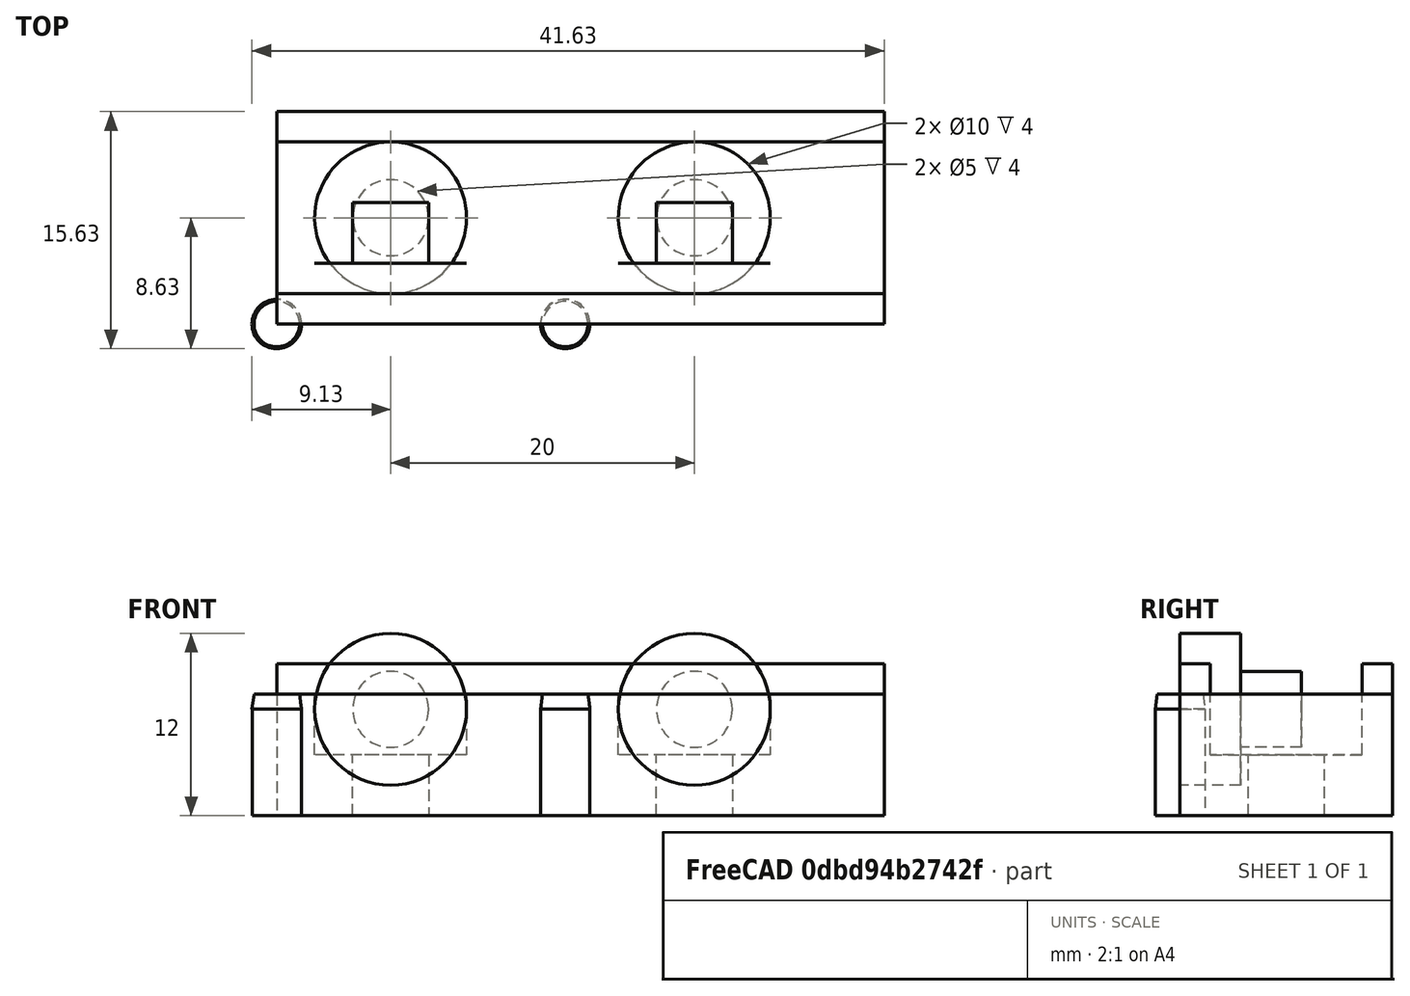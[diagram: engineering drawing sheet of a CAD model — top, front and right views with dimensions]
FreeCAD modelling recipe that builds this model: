
FCSTD DOCUMENT  (FreeCAD 0.21R33771 (Git))
Label: liebherr-fridge-freezer-door-sensor
License: CC BY-SA 4.0
LicenseURL: https://creativecommons.org/licenses/by-sa/4.0/
objects: Part::Cylinder×6, Part::Part2DObjectPython×4, Part::Box×3, App::Part×3, App::DocumentObjectGroup×2, PartDesign::AdditiveLoft×2, PartDesign::Body×2, Part::Cut×1
note: 20 computed .brp shape members not serialized (recipe doc carries the construction recipe); baked Part::Feature solids carry a one-line shape summary decoded from their .brp

FEATURE [Part::Box] Box  label="Block"
  AttacherType = Attacher::AttachEngine3D
  Height = 14
  Length = 40
  Width = 8
FEATURE [Part::Cylinder] Cylinder  label="Left screw hole (rear)"
  Angle = 360
  AttacherType = Attacher::AttachEngine3D
  FirstAngle = 0
  Height = 4
  Placement = pos=(7.5,4,7) rot=(1,0,0;4.71239rad)
  Radius = 2.5
  SecondAngle = 0
FEATURE [Part::Cylinder] Cylinder001  label="Right screw hole (rear)"
  Angle = 360
  AttacherType = Attacher::AttachEngine3D
  FirstAngle = 0
  Height = 4
  Placement = pos=(27.5,4,7) rot=(-1,0,0;1.5708rad)
  Radius = 2.5
  SecondAngle = 0
FEATURE [Part::Cylinder] Cylinder002  label="Left screw hole (front)"
  Angle = 360
  AttacherType = Attacher::AttachEngine3D
  FirstAngle = 0
  Height = 4
  Placement = pos=(7.5,0,7) rot=(-1,0,0;1.5708rad)
  Radius = 5
  SecondAngle = 0
FEATURE [App::DocumentObjectGroup] Group  label="Left screw hole"
  Group = -> [Cylinder,Cylinder002]
FEATURE [Part::Cylinder] Cylinder003  label="Right screw hole (front)"
  Angle = 360
  AttacherType = Attacher::AttachEngine3D
  FirstAngle = 0
  Height = 4
  Placement = pos=(27.5,0,7) rot=(-1,0,0;1.5708rad)
  Radius = 5
  SecondAngle = 0
FEATURE [App::DocumentObjectGroup] Group001  label="Right screw hole"
  Group = -> [Cylinder001,Cylinder003]
FEATURE [App::Part] Part  label="Screw holes"
  Group = -> [Cylinder,Cylinder002,Group,Cylinder001,Cylinder003,Group001]
  Origin = -> Origin
FEATURE [Part::Cut] Cut  label="Cut screw holes"
  Base = -> Box
  Placement = pos=(0,0,8) rot=(1,0,0;4.71239rad)
  Tool = -> Part
FEATURE [Part::Cylinder] Cylinder004  label="Left post"
  Angle = 360
  AttacherType = Attacher::AttachEngine3D
  FirstAngle = 0
  Height = 7
  Radius = 1.625
  SecondAngle = 0
FEATURE [Part::Cylinder] Cylinder005  label="Right post"
  Angle = 360
  AttacherType = Attacher::AttachEngine3D
  FirstAngle = 0
  Height = 7
  Placement = pos=(19,0,0) rot=(0,0,1;0rad)
  Radius = 1.625
  SecondAngle = 0
FEATURE [Part::Part2DObjectPython] Circle  label="Left post (rear)"  # Draft 2D object (typed FeaturePython)
  Area = 8.3469
  FirstAngle = 0
  LastAngle = 0
  MakeFace = true
  Placement = pos=(0,0,7) rot=(0,0,1;0rad)
  Radius = 1.63
FEATURE [Part::Part2DObjectPython] Circle001  label="Right post (rear)"  # Draft 2D object (typed FeaturePython)
  Area = 8.3469
  FirstAngle = 0
  LastAngle = 0
  MakeFace = true
  Placement = pos=(19,0,7) rot=(0,0,1;0rad)
  Radius = 1.63
FEATURE [Part::Part2DObjectPython] Circle002  label="Left post (front)"  # Draft 2D object (typed FeaturePython)
  Area = 7.06858
  FirstAngle = 0
  LastAngle = 0
  MakeFace = true
  Placement = pos=(0,0,8) rot=(0,0,1;0rad)
  Radius = 1.5
FEATURE [Part::Part2DObjectPython] Circle003  label="Right post (front)"  # Draft 2D object (typed FeaturePython)
  Area = 7.06858
  FirstAngle = 0
  LastAngle = 0
  MakeFace = true
  Placement = pos=(19,0,8) rot=(0,0,1;0rad)
  Radius = 1.5
FEATURE [PartDesign::AdditiveLoft] AdditiveLoft  label="Left post (loft)"
  Closed = false
  Placement = pos=(0,0,8) rot=(0,0,1;0rad)
  Profile = -> Circle002
  Ruled = false
  Sections = -> [Circle]
FEATURE [PartDesign::Body] Body  label="Left post (body)"
  Group = -> [Circle002,Circle,AdditiveLoft]
  Origin = -> Origin002
  Tip = -> AdditiveLoft
FEATURE [PartDesign::AdditiveLoft] AdditiveLoft001  label="Right post (loft)"
  Closed = false
  Placement = pos=(19,0,8) rot=(0,0,1;0rad)
  Profile = -> Circle003
  Ruled = false
  Sections = -> [Circle001]
FEATURE [PartDesign::Body] Body001  label="Right post (body)"
  Group = -> [Circle003,Circle001,AdditiveLoft001]
  Origin = -> Origin003
  Tip = -> AdditiveLoft001
FEATURE [App::Part] Part001  label="Posts"
  Group = -> [Cylinder004,Cylinder005,Body,Body001]
  Origin = -> Origin001
  Placement = pos=(16,7,8) rot=(0,0,1;0rad)
FEATURE [Part::Box] Box001  label="Guard (top)"
  AttacherType = Attacher::AttachEngine3D
  Height = 2
  Length = 40
  Placement = pos=(0,12,8) rot=(0,0,1;0rad)
  Width = 2
FEATURE [Part::Box] Box002  label="Guard (bottom)"
  AttacherType = Attacher::AttachEngine3D
  Height = 2
  Length = 40
  Placement = pos=(0,0,8) rot=(0,0,1;0rad)
  Width = 2
FEATURE [App::Part] Part002  label="Main"
  Group = -> [Box,Part,Cut,Box001,Box002]
  Origin = -> Origin005
